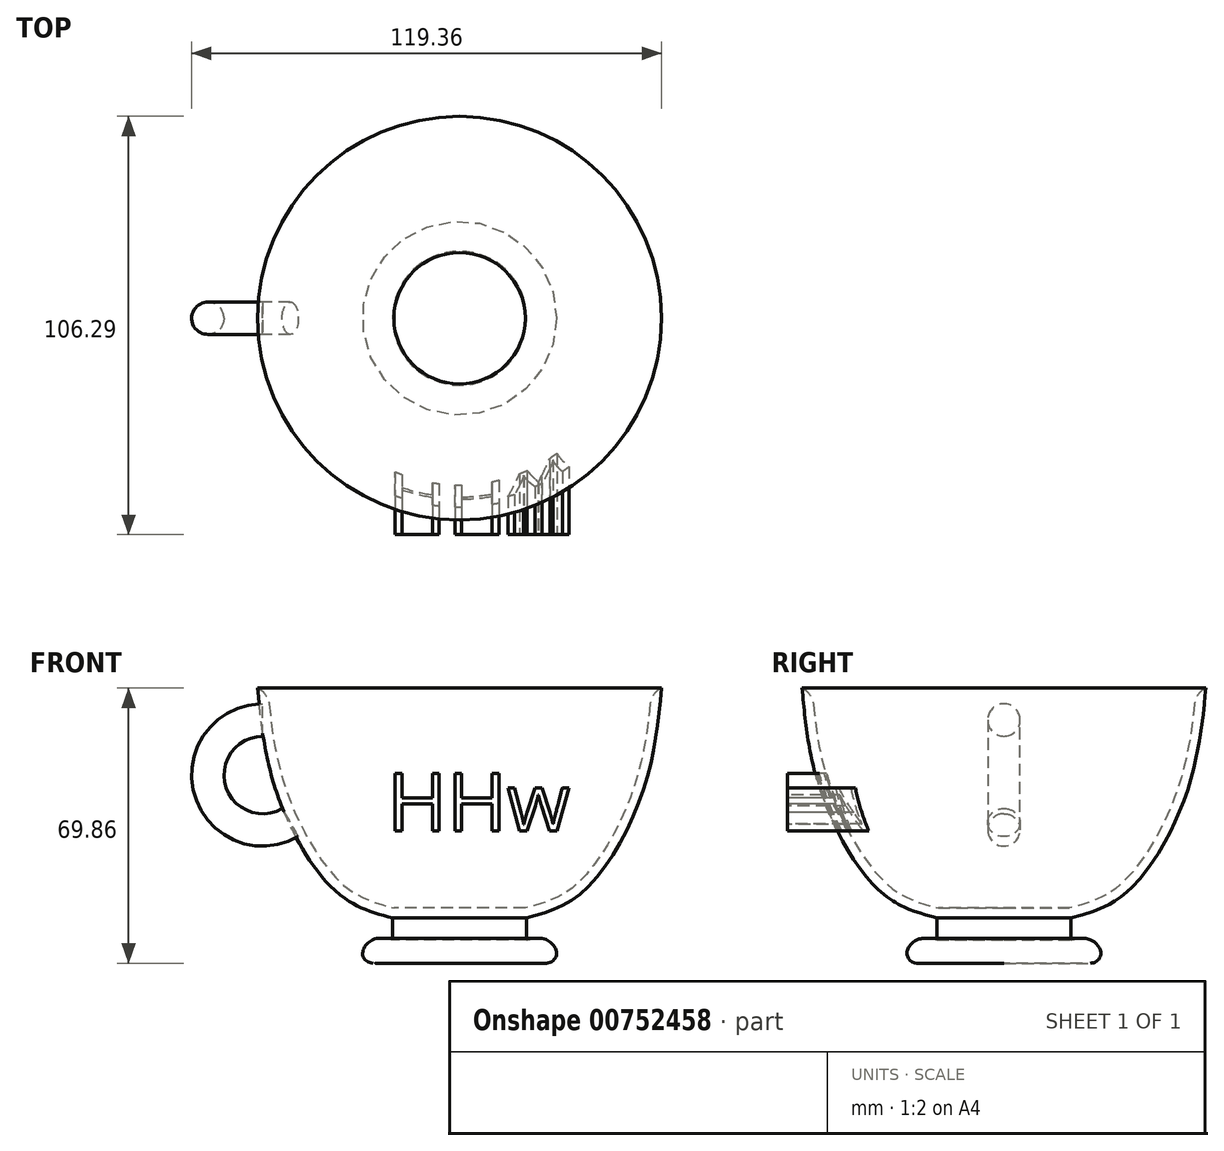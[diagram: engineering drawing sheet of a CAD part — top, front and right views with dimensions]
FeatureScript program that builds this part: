
annotation { "Feature Type Name" : "Feature", "Feature Type Description" : "" }
export const myFeature = defineFeature(function(context is Context, id is Id, definition is map)
    precondition{}
    {
        {
            var Q0;
            Q0=qCreatedBy(makeId("Front.planeOp"),FACE);
            var sketch = newSketch(context, id + "F0", { "sketchPlane" : qUnion([Q0])});
            skLineSegment(sketch, "E0", {"start": v(0, 36.32) * mm, "end": v(51.3, 36.32) * mm});
            skFitSpline(sketch, "E1", {"points": [v(51.3, 36.32) * mm, v(46.54, 10) * mm, v(31, -15.7) * mm, v(17.02, -22.03) * mm], "startDerivative": vector(-6.88, -72.25) * mm, "endDerivative": vector(-52.7, -13.87) * mm});
            skLineSegment(sketch, "E2", {"start": v(17.02, -22.03) * mm, "end": v(17.02, -27.63) * mm});
            skFitSpline(sketch, "E3", {"points": [v(17.02, -27.63) * mm, v(22.12, -27.63) * mm, v(24.63, -31.2) * mm, v(22.03, -33.54) * mm], "startDerivative": vector(14.82, 3.03) * mm, "endDerivative": vector(-14.34, 0) * mm});
            skLineSegment(sketch, "E4", {"start": v(22.03, -33.54) * mm, "end": v(0, -33.54) * mm});
            skLineSegment(sketch, "E5", {"start": v(0, 49) * mm, "end": v(0, -48.68) * mm});
            skLineSegment(sketch, "E6", {"start": v(17.02, -22.03) * mm, "end": v(0, -22.03) * mm});
            skSolve(sketch);
        }
        {
            var Q0;
            {var subQ0=sQuery(id+"F0.wireOp",EDGE,"E0");Q0=makeQuery(id+"F0.imprint","IMPRINT",FACE,{"disambiguationData":[TD([[makeQuery(id+"F0.imprint","IMPRINT",EDGE,{"derivedFrom":subQ0}),-1.0]])]});}
            var Q1;
            Q1=sQuery(id+"F0.wireOp",EDGE,"E5");
            revolve(context, id + "F1", {"surfaceOperationType" : NewSurfaceOperationType.NEW, "entities" : qUnion([Q0]), "axis" : qUnion([Q1]), "revolveType" : RevolveType.FULL});
        }
        {
            var Q0;
            Q0=makeQuery(id+"F1.opRevolve","SWEPT_FACE",FACE,{"disambiguationData":[OSD([sQuery(id+"F0.wireOp",EDGE,"E0")])]});
            shell(context, id + "F2", {"entities" : qUnion([Q0]), "thickness" : 2.5 * mm});
        }
        {
            var Q0;
            Q0=makeQuery(id+"F0.imprint","IMPRINT",FACE,{"disambiguationData":[TD([[makeQuery(id+"F0.imprint","IMPRINT",EDGE,{"derivedFrom":sQuery(id+"F0.wireOp",EDGE,"E2")}),-1.0]])]});
            var Q1;
            Q1=sQuery(id+"F0.wireOp",EDGE,"E5");
            revolve(context, id + "F3", {"operationType" : NewBodyOperationType.ADD, "surfaceOperationType" : NewSurfaceOperationType.NEW, "entities" : qUnion([Q0]), "axis" : qUnion([Q1]), "revolveType" : RevolveType.FULL});
        }
        {
            var Q0;
            Q0=qCreatedBy(makeId("Right.planeOp"),FACE);
            cPlane(context, id + "F4", {"entities" : qUnion([Q0]), "cplaneType" : CPlaneType.OFFSET, "offset" : 50 * mm, "oppositeDirection" : true, "width" : 150 * mm, "height" : 150 * mm});
        }
        {
            var Q0;
            Q0=qCreatedBy(id+"F4.planeOp",FACE);
            var sketch = newSketch(context, id + "F5", { "sketchPlane" : qUnion([Q0])});
            skCircle(sketch, "E7", {"center": v(0, 28.23) * mm, "radius": 4.11 * mm});
            skLineSegment(sketch, "E8", {"start": v(5.55, 14.27) * mm, "end": v(-7.14, 14.27) * mm});
            skSolve(sketch);
        }
        {
            var Q0;
            Q0=makeQuery(id+"F5.imprint","IMPRINT",FACE,{"disambiguationData":[TD([[makeQuery(id+"F5.imprint","IMPRINT",EDGE,{"derivedFrom":sQuery(id+"F5.wireOp",EDGE,"E7")}),1.0]])]});
            var Q1;
            Q1=sQuery(id+"F5.wireOp",EDGE,"E8");
            revolve(context, id + "F6", {"surfaceOperationType" : NewSurfaceOperationType.NEW, "entities" : qUnion([Q0]), "axis" : qUnion([Q1]), "revolveType" : RevolveType.ONE_DIRECTION, "angle" : 210 * degree});
        }
        {
            var Q0;
            Q0=makeQuery(id+"F2.opShell","OFFSET_EDGE",EDGE,{"disambiguationData":[OSD([sQuery(id+"F0.wireOp",EDGE,"E0"),sQuery(id+"F0.wireOp",EDGE,"E1")])]});
            fillet(context, id + "F7", {"entities" : qUnion([Q0]), "radius" : 5 * mm, "tangentPropagation" : true, "allowEdgeOverflow" : false});
        }
        {
            var Q0;
            Q0=qCreatedBy(makeId("Front.planeOp"),FACE);
            cPlane(context, id + "F8", {"entities" : qUnion([Q0]), "cplaneType" : CPlaneType.OFFSET, "offset" : 55 * mm, "width" : 150 * mm, "height" : 150 * mm});
        }
        {
            var Q0;
            Q0=qCreatedBy(id+"F8.planeOp",FACE);
            var sketch = newSketch(context, id + "F9", { "sketchPlane" : qUnion([Q0])});
            skText(sketch, "E9", { "text": "HHw", "fontName": "OpenSans-Regular.ttf"});
            const initialGuessF9  = {"E9": [-0.0184, 0, 1, 0, 0.01484]};
            skSetInitialGuess(sketch, initialGuessF9);
            skSolve(sketch);
        }
        {
            var Q0;
            Q0 = qSketchRegion(id + "F9", true);
            extrude(context, id + "F10", {"entities" : qUnion([Q0]), "operationType" : NewBodyOperationType.ADD, "endBound" : BoundingType.UP_TO_NEXT, "oppositeDirection" : true, "depth" : 25 * mm, "offsetDistance" : 25 * mm});
        }
    });
